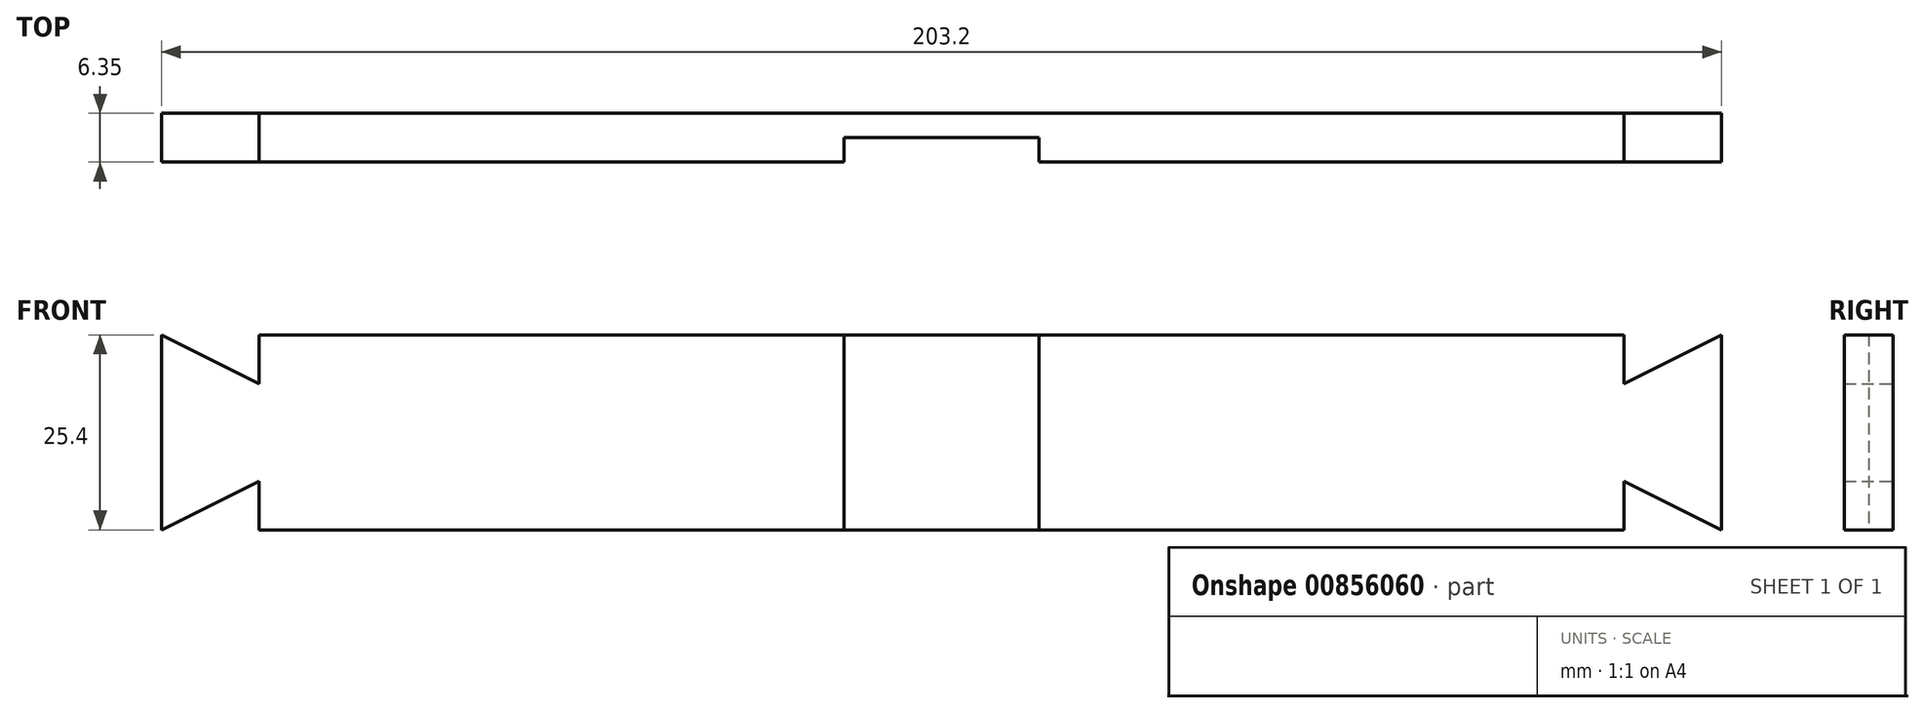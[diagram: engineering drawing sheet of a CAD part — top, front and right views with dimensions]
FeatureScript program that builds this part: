
annotation { "Feature Type Name" : "Feature", "Feature Type Description" : "" }
export const myFeature = defineFeature(function(context is Context, id is Id, definition is map)
    precondition{}
    {
        {
            var Q0;
            Q0=qCreatedBy(makeId("Front.planeOp"),FACE);
            var sketch = newSketch(context, id + "F0", { "sketchPlane" : qUnion([Q0])});
            skLineSegment(sketch, "E0.bottom", {"start": v(-98.13, -19.3) * mm, "end": v(105.07, -19.3) * mm});
            skLineSegment(sketch, "E0.top", {"start": v(-98.13, -44.7) * mm, "end": v(105.07, -44.7) * mm});
            skLineSegment(sketch, "E0.left", {"start": v(-98.13, -19.3) * mm, "end": v(-98.13, -44.7) * mm});
            skLineSegment(sketch, "E0.right", {"start": v(105.07, -19.3) * mm, "end": v(105.07, -44.7) * mm});
            skLineSegment(sketch, "E1", {"start": v(-85.43, -19.3) * mm, "end": v(-85.43, -25.66) * mm});
            skLineSegment(sketch, "E2", {"start": v(-85.43, -25.66) * mm, "end": v(-98.13, -19.3) * mm});
            skLineSegment(sketch, "E3", {"start": v(-98.13, -44.7) * mm, "end": v(-85.43, -38.36) * mm});
            skLineSegment(sketch, "E4", {"start": v(-85.43, -38.36) * mm, "end": v(-85.43, -44.7) * mm});
            skLineSegment(sketch, "E5", {"start": v(92.37, -19.3) * mm, "end": v(92.37, -25.66) * mm});
            skLineSegment(sketch, "E6", {"start": v(92.37, -25.66) * mm, "end": v(105.07, -19.3) * mm});
            skLineSegment(sketch, "E7", {"start": v(105.07, -44.7) * mm, "end": v(92.37, -38.36) * mm});
            skLineSegment(sketch, "E8", {"start": v(92.37, -38.36) * mm, "end": v(92.37, -44.7) * mm});
            skSolve(sketch);
        }
        {
            var Q0;
            {var subQ1=sQuery(id+"F0.wireOp",EDGE,"E1");Q0=makeQuery(id+"F0.imprint","IMPRINT",FACE,{"disambiguationData":[TD([[makeQuery(id+"F0.imprint","IMPRINT",EDGE,{"derivedFrom":subQ1}),1.0]])]});}
            extrude(context, id + "F1", {"entities" : qUnion([Q0]), "depth" : 6.35 * mm, "offsetDistance" : 25.4 * mm});
        }
        {
            var Q0;
            Q0=makeQuery(id+"F1.opExtrude","CAP_FACE",FACE,{"disambiguationData":[OSD([sQuery(id+"F0.wireOp",EDGE,"E0.bottom"),sQuery(id+"F0.wireOp",EDGE,"E0.top"),sQuery(id+"F0.wireOp",EDGE,"E1"),sQuery(id+"F0.wireOp",EDGE,"E2"),sQuery(id+"F0.wireOp",EDGE,"E0.left"),sQuery(id+"F0.wireOp",EDGE,"E3"),sQuery(id+"F0.wireOp",EDGE,"E4"),sQuery(id+"F0.wireOp",EDGE,"E5"),sQuery(id+"F0.wireOp",EDGE,"E6"),sQuery(id+"F0.wireOp",EDGE,"E0.right"),sQuery(id+"F0.wireOp",EDGE,"E7"),sQuery(id+"F0.wireOp",EDGE,"E8")])],"isStart":false});
            var sketch = newSketch(context, id + "F2", { "sketchPlane" : qUnion([Q0])});
            skLineSegment(sketch, "E9.bottom", {"start": v(-9.23, -19.3) * mm, "end": v(16.17, -19.3) * mm});
            skLineSegment(sketch, "E9.top", {"start": v(-9.23, -44.7) * mm, "end": v(16.17, -44.7) * mm});
            skLineSegment(sketch, "E9.left", {"start": v(-9.23, -19.3) * mm, "end": v(-9.23, -44.7) * mm});
            skLineSegment(sketch, "E9.right", {"start": v(16.17, -19.3) * mm, "end": v(16.17, -44.7) * mm});
            skLineSegment(sketch, "E10", {"start": v(-9.23, -32) * mm, "end": v(-98.13, -32) * mm});
            skLineSegment(sketch, "E11", {"start": v(16.17, -32) * mm, "end": v(105.07, -32) * mm});
            skSolve(sketch);
        }
        {
            var Q0;
            {var subQ4=sQuery(id+"F2.wireOp",EDGE,"E9.bottom");Q0=makeQuery(id+"F2.imprint","IMPRINT",FACE,{"disambiguationData":[TD([[makeQuery(id+"F2.imprint","IMPRINT",EDGE,{"derivedFrom":subQ4}),-1.0]])]});}
            extrude(context, id + "F3", {"entities" : qUnion([Q0]), "operationType" : NewBodyOperationType.REMOVE, "oppositeDirection" : true, "depth" : 3.17 * mm, "offsetDistance" : 25.4 * mm});
        }
    });
